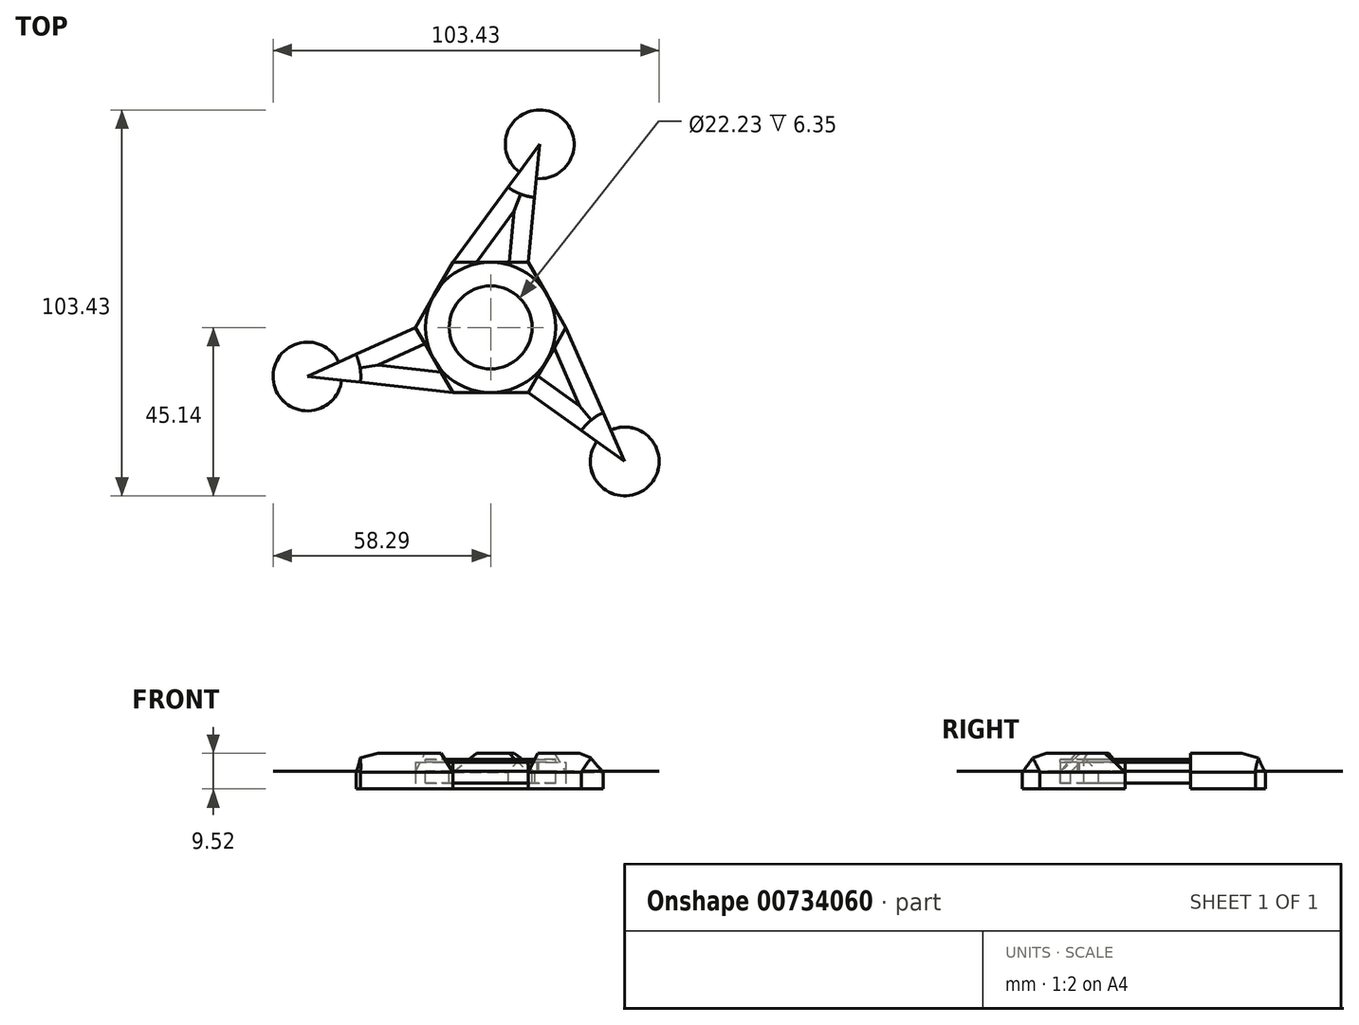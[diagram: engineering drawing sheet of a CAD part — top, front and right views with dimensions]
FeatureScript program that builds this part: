
annotation { "Feature Type Name" : "Feature", "Feature Type Description" : "" }
export const myFeature = defineFeature(function(context is Context, id is Id, definition is map)
    precondition{}
    {
        {
            var Q0;
            Q0=qCreatedBy(makeId("Top.planeOp"),FACE);
            var sketch = newSketch(context, id + "F0", { "sketchPlane" : qUnion([Q0])});
            skCircle(sketch, "E0", {"center": v(0, 0) * mm, "radius": 11.11 * mm});
            skCircle(sketch, "E1", {"center": v(0, 0) * mm, "radius": 17.46 * mm});
            skPoint(sketch, "E2.0.midPoint", {"position": v(15.12, 8.73) * mm});
            skCircle(sketch, "E3.cCircle", {"center": v(0, 0) * mm, "radius": 17.46 * mm, "construction": true});
            skLineSegment(sketch, "E3.0", {"start": v(10.08, 17.46) * mm, "end": v(20.16, 0) * mm});
            skLineSegment(sketch, "E3.1", {"start": v(20.16, 0) * mm, "end": v(10.08, -17.46) * mm});
            skLineSegment(sketch, "E3.2", {"start": v(10.08, -17.46) * mm, "end": v(-10.08, -17.46) * mm});
            skLineSegment(sketch, "E3.3", {"start": v(-10.08, -17.46) * mm, "end": v(-20.16, 0) * mm});
            skLineSegment(sketch, "E3.4", {"start": v(-20.16, 0) * mm, "end": v(-10.08, 17.46) * mm});
            skLineSegment(sketch, "E3.5", {"start": v(-10.08, 17.46) * mm, "end": v(10.08, 17.46) * mm});
            skLineSegment(sketch, "E4", {"start": v(-10.08, 17.46) * mm, "end": v(13.15, 49.07) * mm});
            skLineSegment(sketch, "E5", {"start": v(13.15, 49.07) * mm, "end": v(10.08, 17.46) * mm});
            skLineSegment(sketch, "E6", {"start": v(13.15, 49.07) * mm, "end": v(-13.15, -49.07) * mm});
            skLineSegment(sketch, "E7", {"start": v(-20.16, 0) * mm, "end": v(-49.07, -13.15) * mm});
            skLineSegment(sketch, "E8", {"start": v(-49.07, -13.15) * mm, "end": v(-10.08, -17.46) * mm});
            skLineSegment(sketch, "E9", {"start": v(-49.07, -13.15) * mm, "end": v(49.07, 13.15) * mm});
            skLineSegment(sketch, "E10", {"start": v(10.08, -17.46) * mm, "end": v(35.92, -35.92) * mm});
            skLineSegment(sketch, "E11", {"start": v(35.92, -35.92) * mm, "end": v(20.16, 0) * mm});
            skLineSegment(sketch, "E12", {"start": v(35.92, -35.92) * mm, "end": v(-35.92, 35.92) * mm});
            skCircle(sketch, "E13", {"center": v(-49.07, -13.15) * mm, "radius": 14.29 * mm});
            skCircle(sketch, "E14", {"center": v(35.92, -35.92) * mm, "radius": 14.29 * mm});
            skCircle(sketch, "E15", {"center": v(13.15, 49.07) * mm, "radius": 14.29 * mm});
            skSolve(sketch);
        }
        {
            var Q0;
            {var subQ0=sQuery(id+"F0.wireOp",EDGE,"E9");var subQ1=sQuery(id+"F0.wireOp",EDGE,"E0");var subQ2=makeQuery(id+"F0.imprint","INTERSECT",VERTEX,{"disambiguationData":[OD(1.0)],"derivedFrom":[subQ1,subQ0]});Q0=makeQuery(id+"F0.imprint","IMPRINT",FACE,{"disambiguationData":[TD([[makeQuery(id+"F0.imprint","IMPRINT",EDGE,{"disambiguationData":[TD([[subQ2,-1.0]])],"derivedFrom":subQ1}),-1.0]])]});}
            var Q1;
            {var subQ0=sQuery(id+"F0.wireOp",EDGE,"E6");var subQ1=sQuery(id+"F0.wireOp",EDGE,"E0");var subQ2=makeQuery(id+"F0.imprint","INTERSECT",VERTEX,{"disambiguationData":[OD(0.0)],"derivedFrom":[subQ1,subQ0]});Q1=makeQuery(id+"F0.imprint","IMPRINT",FACE,{"disambiguationData":[TD([[makeQuery(id+"F0.imprint","IMPRINT",EDGE,{"disambiguationData":[TD([[subQ2,-1.0]])],"derivedFrom":subQ1}),-1.0]])]});}
            var Q2;
            {var subQ0=sQuery(id+"F0.wireOp",EDGE,"E12");var subQ1=sQuery(id+"F0.wireOp",EDGE,"E0");var subQ2=makeQuery(id+"F0.imprint","INTERSECT",VERTEX,{"disambiguationData":[OD(0.0)],"derivedFrom":[subQ1,subQ0]});Q2=makeQuery(id+"F0.imprint","IMPRINT",FACE,{"disambiguationData":[TD([[makeQuery(id+"F0.imprint","IMPRINT",EDGE,{"disambiguationData":[TD([[subQ2,-1.0]])],"derivedFrom":subQ1}),-1.0]])]});}
            var Q3;
            {var subQ0=sQuery(id+"F0.wireOp",EDGE,"E6");var subQ1=sQuery(id+"F0.wireOp",EDGE,"E0");var subQ2=makeQuery(id+"F0.imprint","INTERSECT",VERTEX,{"disambiguationData":[OD(0.0)],"derivedFrom":[subQ1,subQ0]});Q3=makeQuery(id+"F0.imprint","IMPRINT",FACE,{"disambiguationData":[TD([[makeQuery(id+"F0.imprint","IMPRINT",EDGE,{"disambiguationData":[TD([[subQ2,1.0]])],"derivedFrom":subQ1}),-1.0]])]});}
            var Q4;
            {var subQ0=sQuery(id+"F0.wireOp",EDGE,"E9");var subQ1=sQuery(id+"F0.wireOp",EDGE,"E0");var subQ2=makeQuery(id+"F0.imprint","INTERSECT",VERTEX,{"disambiguationData":[OD(0.0)],"derivedFrom":[subQ1,subQ0]});Q4=makeQuery(id+"F0.imprint","IMPRINT",FACE,{"disambiguationData":[TD([[makeQuery(id+"F0.imprint","IMPRINT",EDGE,{"disambiguationData":[TD([[subQ2,1.0]])],"derivedFrom":subQ1}),-1.0]])]});}
            var Q5;
            {var subQ0=sQuery(id+"F0.wireOp",EDGE,"E6");var subQ1=sQuery(id+"F0.wireOp",EDGE,"E0");var subQ2=makeQuery(id+"F0.imprint","INTERSECT",VERTEX,{"disambiguationData":[OD(1.0)],"derivedFrom":[subQ1,subQ0]});Q5=makeQuery(id+"F0.imprint","IMPRINT",FACE,{"disambiguationData":[TD([[makeQuery(id+"F0.imprint","IMPRINT",EDGE,{"disambiguationData":[TD([[subQ2,-1.0]])],"derivedFrom":subQ1}),-1.0]])]});}
            extrude(context, id + "F1", {"entities" : qUnion([Q0, Q1, Q2, Q3, Q4, Q5]), "oppositeDirection" : true, "depth" : 3.17 * mm, "offsetDistance" : 25.4 * mm, "hasSecondDirection" : true, "secondDirectionOppositeDirection" : false, "secondDirectionDepth" : 3.17 * mm});
        }
        {
            var Q0;
            {var subQ0=sQuery(id+"F0.wireOp",EDGE,"E3.0");var subQ1=sQuery(id+"F0.wireOp",EDGE,"E1");var subQ2=makeQuery(id+"F0.imprint","INTERSECT",VERTEX,{"derivedFrom":[subQ1,subQ0]});Q0=makeQuery(id+"F0.imprint","IMPRINT",FACE,{"disambiguationData":[TD([[makeQuery(id+"F0.imprint","IMPRINT",EDGE,{"disambiguationData":[TD([[subQ2,-1.0]])],"derivedFrom":subQ1}),-1.0]])]});}
            var Q1;
            {var subQ0=sQuery(id+"F0.wireOp",EDGE,"E9");var subQ1=sQuery(id+"F0.wireOp",EDGE,"E1");var subQ2=makeQuery(id+"F0.imprint","INTERSECT",VERTEX,{"disambiguationData":[OD(0.0)],"derivedFrom":[subQ1,subQ0]});Q1=makeQuery(id+"F0.imprint","IMPRINT",FACE,{"disambiguationData":[TD([[makeQuery(id+"F0.imprint","IMPRINT",EDGE,{"disambiguationData":[TD([[subQ2,1.0]])],"derivedFrom":subQ1}),-1.0]])]});}
            var Q2;
            {var subQ0=sQuery(id+"F0.wireOp",EDGE,"E3.2");var subQ1=sQuery(id+"F0.wireOp",EDGE,"E1");var subQ2=makeQuery(id+"F0.imprint","INTERSECT",VERTEX,{"derivedFrom":[subQ1,subQ0]});Q2=makeQuery(id+"F0.imprint","IMPRINT",FACE,{"disambiguationData":[TD([[makeQuery(id+"F0.imprint","IMPRINT",EDGE,{"disambiguationData":[TD([[subQ2,-1.0]])],"derivedFrom":subQ1}),-1.0]])]});}
            var Q3;
            {var subQ0=sQuery(id+"F0.wireOp",EDGE,"E3.3");var subQ1=sQuery(id+"F0.wireOp",EDGE,"E1");var subQ2=makeQuery(id+"F0.imprint","INTERSECT",VERTEX,{"derivedFrom":[subQ1,subQ0]});Q3=makeQuery(id+"F0.imprint","IMPRINT",FACE,{"disambiguationData":[TD([[makeQuery(id+"F0.imprint","IMPRINT",EDGE,{"disambiguationData":[TD([[subQ2,-1.0]])],"derivedFrom":subQ1}),-1.0]])]});}
            var Q4;
            {var subQ0=sQuery(id+"F0.wireOp",EDGE,"E3.4");var subQ1=sQuery(id+"F0.wireOp",EDGE,"E1");var subQ2=makeQuery(id+"F0.imprint","INTERSECT",VERTEX,{"derivedFrom":[subQ1,subQ0]});Q4=makeQuery(id+"F0.imprint","IMPRINT",FACE,{"disambiguationData":[TD([[makeQuery(id+"F0.imprint","IMPRINT",EDGE,{"disambiguationData":[TD([[subQ2,-1.0]])],"derivedFrom":subQ1}),-1.0]])]});}
            var Q5;
            {var subQ0=sQuery(id+"F0.wireOp",EDGE,"E3.5");var subQ1=sQuery(id+"F0.wireOp",EDGE,"E1");var subQ2=makeQuery(id+"F0.imprint","INTERSECT",VERTEX,{"derivedFrom":[subQ1,subQ0]});Q5=makeQuery(id+"F0.imprint","IMPRINT",FACE,{"disambiguationData":[TD([[makeQuery(id+"F0.imprint","IMPRINT",EDGE,{"disambiguationData":[TD([[subQ2,-1.0]])],"derivedFrom":subQ1}),-1.0]])]});}
            var Q6;
            {var subQ0=sQuery(id+"F0.wireOp",EDGE,"E3.4");var subQ1=sQuery(id+"F0.wireOp",EDGE,"E1");var subQ2=makeQuery(id+"F0.imprint","INTERSECT",VERTEX,{"derivedFrom":[subQ1,subQ0]});Q6=makeQuery(id+"F0.imprint","IMPRINT",FACE,{"disambiguationData":[TD([[makeQuery(id+"F0.imprint","IMPRINT",EDGE,{"disambiguationData":[TD([[subQ2,1.0]])],"derivedFrom":subQ1}),-1.0]])]});}
            var Q7;
            {var subQ0=sQuery(id+"F0.wireOp",EDGE,"E9");var subQ1=sQuery(id+"F0.wireOp",EDGE,"E1");var subQ2=makeQuery(id+"F0.imprint","INTERSECT",VERTEX,{"disambiguationData":[OD(1.0)],"derivedFrom":[subQ1,subQ0]});Q7=makeQuery(id+"F0.imprint","IMPRINT",FACE,{"disambiguationData":[TD([[makeQuery(id+"F0.imprint","IMPRINT",EDGE,{"disambiguationData":[TD([[subQ2,-1.0]])],"derivedFrom":subQ1}),-1.0]])]});}
            var Q8;
            {var subQ0=sQuery(id+"F0.wireOp",EDGE,"E3.2");var subQ1=sQuery(id+"F0.wireOp",EDGE,"E1");var subQ2=makeQuery(id+"F0.imprint","INTERSECT",VERTEX,{"derivedFrom":[subQ1,subQ0]});Q8=makeQuery(id+"F0.imprint","IMPRINT",FACE,{"disambiguationData":[TD([[makeQuery(id+"F0.imprint","IMPRINT",EDGE,{"disambiguationData":[TD([[subQ2,1.0]])],"derivedFrom":subQ1}),-1.0]])]});}
            var Q9;
            {var subQ0=sQuery(id+"F0.wireOp",EDGE,"E12");var subQ1=sQuery(id+"F0.wireOp",EDGE,"E1");var subQ2=makeQuery(id+"F0.imprint","INTERSECT",VERTEX,{"disambiguationData":[OD(1.0)],"derivedFrom":[subQ1,subQ0]});Q9=makeQuery(id+"F0.imprint","IMPRINT",FACE,{"disambiguationData":[TD([[makeQuery(id+"F0.imprint","IMPRINT",EDGE,{"disambiguationData":[TD([[subQ2,-1.0]])],"derivedFrom":subQ1}),-1.0]])]});}
            var Q10;
            {var subQ0=sQuery(id+"F0.wireOp",EDGE,"E3.0");var subQ1=sQuery(id+"F0.wireOp",EDGE,"E1");var subQ2=makeQuery(id+"F0.imprint","INTERSECT",VERTEX,{"derivedFrom":[subQ1,subQ0]});Q10=makeQuery(id+"F0.imprint","IMPRINT",FACE,{"disambiguationData":[TD([[makeQuery(id+"F0.imprint","IMPRINT",EDGE,{"disambiguationData":[TD([[subQ2,1.0]])],"derivedFrom":subQ1}),-1.0]])]});}
            var Q11;
            {var subQ0=sQuery(id+"F0.wireOp",EDGE,"E6");var subQ1=sQuery(id+"F0.wireOp",EDGE,"E1");var subQ2=makeQuery(id+"F0.imprint","INTERSECT",VERTEX,{"disambiguationData":[OD(0.0)],"derivedFrom":[subQ1,subQ0]});Q11=makeQuery(id+"F0.imprint","IMPRINT",FACE,{"disambiguationData":[TD([[makeQuery(id+"F0.imprint","IMPRINT",EDGE,{"disambiguationData":[TD([[subQ2,-1.0]])],"derivedFrom":subQ1}),-1.0]])]});}
            extrude(context, id + "F2", {"entities" : qUnion([Q0, Q1, Q2, Q3, Q4, Q5, Q6, Q7, Q8, Q9, Q10, Q11]), "operationType" : NewBodyOperationType.ADD, "depth" : 2.38 * mm, "offsetDistance" : 25.4 * mm, "hasSecondDirection" : true, "secondDirectionOppositeDirection" : true, "secondDirectionDepth" : 3 / 812.8 * mm});
        }
        {
            var Q0;
            {var subQ0=sQuery(id+"F0.wireOp",EDGE,"E10");var subQ5=sQuery(id+"F0.wireOp",EDGE,"E14");var subQ6=makeQuery(id+"F0.imprint","INTERSECT",VERTEX,{"derivedFrom":[subQ0,subQ5]});Q0=makeQuery(id+"F0.imprint","IMPRINT",FACE,{"disambiguationData":[TD([[makeQuery(id+"F0.imprint","IMPRINT",EDGE,{"disambiguationData":[TD([[subQ6,1.0]])],"derivedFrom":subQ5}),-1.0]])]});}
            var Q1;
            {var subQ0=sQuery(id+"F0.wireOp",EDGE,"E11");var subQ5=sQuery(id+"F0.wireOp",EDGE,"E14");var subQ7=makeQuery(id+"F0.imprint","INTERSECT",VERTEX,{"derivedFrom":[subQ0,subQ5]});Q1=makeQuery(id+"F0.imprint","IMPRINT",FACE,{"disambiguationData":[TD([[makeQuery(id+"F0.imprint","IMPRINT",EDGE,{"disambiguationData":[TD([[subQ7,-1.0]])],"derivedFrom":subQ5}),-1.0]])]});}
            var Q2;
            {var subQ0=sQuery(id+"F0.wireOp",EDGE,"E5");var subQ5=sQuery(id+"F0.wireOp",EDGE,"E15");var subQ6=makeQuery(id+"F0.imprint","INTERSECT",VERTEX,{"derivedFrom":[subQ0,subQ5]});Q2=makeQuery(id+"F0.imprint","IMPRINT",FACE,{"disambiguationData":[TD([[makeQuery(id+"F0.imprint","IMPRINT",EDGE,{"disambiguationData":[TD([[subQ6,1.0]])],"derivedFrom":subQ5}),-1.0]])]});}
            var Q3;
            {var subQ0=sQuery(id+"F0.wireOp",EDGE,"E4");var subQ5=sQuery(id+"F0.wireOp",EDGE,"E15");var subQ6=makeQuery(id+"F0.imprint","INTERSECT",VERTEX,{"derivedFrom":[subQ0,subQ5]});Q3=makeQuery(id+"F0.imprint","IMPRINT",FACE,{"disambiguationData":[TD([[makeQuery(id+"F0.imprint","IMPRINT",EDGE,{"disambiguationData":[TD([[subQ6,-1.0]])],"derivedFrom":subQ5}),-1.0]])]});}
            var Q4;
            {var subQ0=sQuery(id+"F0.wireOp",EDGE,"E8");var subQ5=sQuery(id+"F0.wireOp",EDGE,"E13");var subQ6=makeQuery(id+"F0.imprint","INTERSECT",VERTEX,{"derivedFrom":[subQ0,subQ5]});Q4=makeQuery(id+"F0.imprint","IMPRINT",FACE,{"disambiguationData":[TD([[makeQuery(id+"F0.imprint","IMPRINT",EDGE,{"disambiguationData":[TD([[subQ6,-1.0]])],"derivedFrom":subQ5}),-1.0]])]});}
            var Q5;
            {var subQ0=sQuery(id+"F0.wireOp",EDGE,"E7");var subQ5=sQuery(id+"F0.wireOp",EDGE,"E13");var subQ6=makeQuery(id+"F0.imprint","INTERSECT",VERTEX,{"derivedFrom":[subQ0,subQ5]});Q5=makeQuery(id+"F0.imprint","IMPRINT",FACE,{"disambiguationData":[TD([[makeQuery(id+"F0.imprint","IMPRINT",EDGE,{"disambiguationData":[TD([[subQ6,1.0]])],"derivedFrom":subQ5}),-1.0]])]});}
            extrude(context, id + "F3", {"entities" : qUnion([Q0, Q1, Q2, Q3, Q4, Q5]), "surfaceOperationType" : NewSurfaceOperationType.ADD, "depth" : 4.76 * mm, "offsetDistance" : 25.4 * mm, "hasSecondDirection" : true, "secondDirectionOppositeDirection" : true, "secondDirectionDepth" : 4.76 * mm});
        }
        {
            var Q0;
            {var subQ1=sQuery(id+"F0.wireOp",EDGE,"E4");var subQ3=sQuery(id+"F0.wireOp",EDGE,"E15");var subQ4=makeQuery(id+"F0.imprint","INTERSECT",VERTEX,{"derivedFrom":[subQ1,subQ3]});Q0=makeQuery(id+"F0.imprint","IMPRINT",FACE,{"disambiguationData":[TD([[makeQuery(id+"F0.imprint","IMPRINT",EDGE,{"disambiguationData":[TD([[subQ4,1.0]])],"derivedFrom":subQ3}),1.0]])]});}
            var Q1;
            {var subQ1=sQuery(id+"F0.wireOp",EDGE,"E7");var subQ3=sQuery(id+"F0.wireOp",EDGE,"E13");var subQ4=makeQuery(id+"F0.imprint","INTERSECT",VERTEX,{"derivedFrom":[subQ1,subQ3]});Q1=makeQuery(id+"F0.imprint","IMPRINT",FACE,{"disambiguationData":[TD([[makeQuery(id+"F0.imprint","IMPRINT",EDGE,{"disambiguationData":[TD([[subQ4,-1.0]])],"derivedFrom":subQ3}),1.0]])]});}
            var Q2;
            {var subQ1=sQuery(id+"F0.wireOp",EDGE,"E10");var subQ3=sQuery(id+"F0.wireOp",EDGE,"E14");var subQ4=makeQuery(id+"F0.imprint","INTERSECT",VERTEX,{"derivedFrom":[subQ1,subQ3]});Q2=makeQuery(id+"F0.imprint","IMPRINT",FACE,{"disambiguationData":[TD([[makeQuery(id+"F0.imprint","IMPRINT",EDGE,{"disambiguationData":[TD([[subQ4,-1.0]])],"derivedFrom":subQ3}),1.0]])]});}
            extrude(context, id + "F4", {"entities" : qUnion([Q0, Q1, Q2]), "depth" : 5 / 812.8 * mm, "offsetDistance" : 25.4 * mm, "hasSecondDirection" : true, "secondDirectionOppositeDirection" : true, "secondDirectionDepth" : 5 / 812.8 * mm});
        }
        {
            var Q0;
            {var subQ1=sQuery(id+"F0.wireOp",EDGE,"E10");var subQ3=sQuery(id+"F0.wireOp",EDGE,"E14");var subQ4=makeQuery(id+"F0.imprint","INTERSECT",VERTEX,{"derivedFrom":[subQ1,subQ3]});Q0=makeQuery(id+"F0.imprint","IMPRINT",FACE,{"disambiguationData":[TD([[makeQuery(id+"F0.imprint","IMPRINT",EDGE,{"disambiguationData":[TD([[subQ4,1.0]])],"derivedFrom":subQ3}),1.0]])]});}
            var Q1;
            {var subQ1=sQuery(id+"F0.wireOp",EDGE,"E11");var subQ3=sQuery(id+"F0.wireOp",EDGE,"E14");var subQ4=makeQuery(id+"F0.imprint","INTERSECT",VERTEX,{"derivedFrom":[subQ1,subQ3]});Q1=makeQuery(id+"F0.imprint","IMPRINT",FACE,{"disambiguationData":[TD([[makeQuery(id+"F0.imprint","IMPRINT",EDGE,{"disambiguationData":[TD([[subQ4,-1.0]])],"derivedFrom":subQ3}),1.0]])]});}
            var Q2;
            {var subQ1=sQuery(id+"F0.wireOp",EDGE,"E5");var subQ3=sQuery(id+"F0.wireOp",EDGE,"E15");var subQ4=makeQuery(id+"F0.imprint","INTERSECT",VERTEX,{"derivedFrom":[subQ1,subQ3]});Q2=makeQuery(id+"F0.imprint","IMPRINT",FACE,{"disambiguationData":[TD([[makeQuery(id+"F0.imprint","IMPRINT",EDGE,{"disambiguationData":[TD([[subQ4,1.0]])],"derivedFrom":subQ3}),1.0]])]});}
            var Q3;
            {var subQ1=sQuery(id+"F0.wireOp",EDGE,"E4");var subQ3=sQuery(id+"F0.wireOp",EDGE,"E15");var subQ4=makeQuery(id+"F0.imprint","INTERSECT",VERTEX,{"derivedFrom":[subQ1,subQ3]});Q3=makeQuery(id+"F0.imprint","IMPRINT",FACE,{"disambiguationData":[TD([[makeQuery(id+"F0.imprint","IMPRINT",EDGE,{"disambiguationData":[TD([[subQ4,-1.0]])],"derivedFrom":subQ3}),1.0]])]});}
            var Q4;
            {var subQ1=sQuery(id+"F0.wireOp",EDGE,"E7");var subQ3=sQuery(id+"F0.wireOp",EDGE,"E13");var subQ4=makeQuery(id+"F0.imprint","INTERSECT",VERTEX,{"derivedFrom":[subQ1,subQ3]});Q4=makeQuery(id+"F0.imprint","IMPRINT",FACE,{"disambiguationData":[TD([[makeQuery(id+"F0.imprint","IMPRINT",EDGE,{"disambiguationData":[TD([[subQ4,1.0]])],"derivedFrom":subQ3}),1.0]])]});}
            var Q5;
            {var subQ1=sQuery(id+"F0.wireOp",EDGE,"E8");var subQ3=sQuery(id+"F0.wireOp",EDGE,"E13");var subQ4=makeQuery(id+"F0.imprint","INTERSECT",VERTEX,{"derivedFrom":[subQ1,subQ3]});Q5=makeQuery(id+"F0.imprint","IMPRINT",FACE,{"disambiguationData":[TD([[makeQuery(id+"F0.imprint","IMPRINT",EDGE,{"disambiguationData":[TD([[subQ4,-1.0]])],"derivedFrom":subQ3}),1.0]])]});}
            extrude(context, id + "F5", {"entities" : qUnion([Q0, Q1, Q2, Q3, Q4, Q5]), "depth" : 3 / 812.8 * mm, "offsetDistance" : 25.4 * mm, "hasSecondDirection" : true, "secondDirectionOppositeDirection" : true, "secondDirectionDepth" : 3 / 812.8 * mm});
        }
        {
            var Q0;
            Q0=makeQuery(id+"F3.opExtrude","CAP_EDGE",EDGE,{"disambiguationData":[OSD([sQuery(id+"F0.wireOp",EDGE,"E11")])],"isStart":false});
            var Q1;
            Q1=makeQuery(id+"F3.opExtrude","CAP_EDGE",EDGE,{"disambiguationData":[OSD([sQuery(id+"F0.wireOp",EDGE,"E10")])],"isStart":false});
            var Q2;
            Q2=makeQuery(id+"F3.opExtrude","CAP_EDGE",EDGE,{"disambiguationData":[OSD([sQuery(id+"F0.wireOp",EDGE,"E5")])],"isStart":false});
            var Q3;
            Q3=makeQuery(id+"F3.opExtrude","CAP_EDGE",EDGE,{"disambiguationData":[OSD([sQuery(id+"F0.wireOp",EDGE,"E4")])],"isStart":false});
            var Q4;
            Q4=makeQuery(id+"F3.opExtrude","CAP_EDGE",EDGE,{"disambiguationData":[OSD([sQuery(id+"F0.wireOp",EDGE,"E7")])],"isStart":false});
            var Q5;
            Q5=makeQuery(id+"F3.opExtrude","CAP_EDGE",EDGE,{"disambiguationData":[OSD([sQuery(id+"F0.wireOp",EDGE,"E8")])],"isStart":false});
            var Q6;
            Q6=makeQuery(id+"F4.opExtrude","CAP_EDGE",EDGE,{"disambiguationData":[OSD([sQuery(id+"F0.wireOp",EDGE,"E14")])],"isStart":false});
            var Q7;
            Q7=makeQuery(id+"F4.opExtrude","CAP_EDGE",EDGE,{"disambiguationData":[OSD([sQuery(id+"F0.wireOp",EDGE,"E15")])],"isStart":false});
            var Q8;
            Q8=makeQuery(id+"F4.opExtrude","CAP_EDGE",EDGE,{"disambiguationData":[OSD([sQuery(id+"F0.wireOp",EDGE,"E13")])],"isStart":false});
            chamfer(context, id + "F6", {"entities" : qUnion([Q0, Q1, Q2, Q3, Q4, Q5, Q6, Q7, Q8]), "width" : 5.08 * mm, "tangentPropagation" : true});
        }
    });
